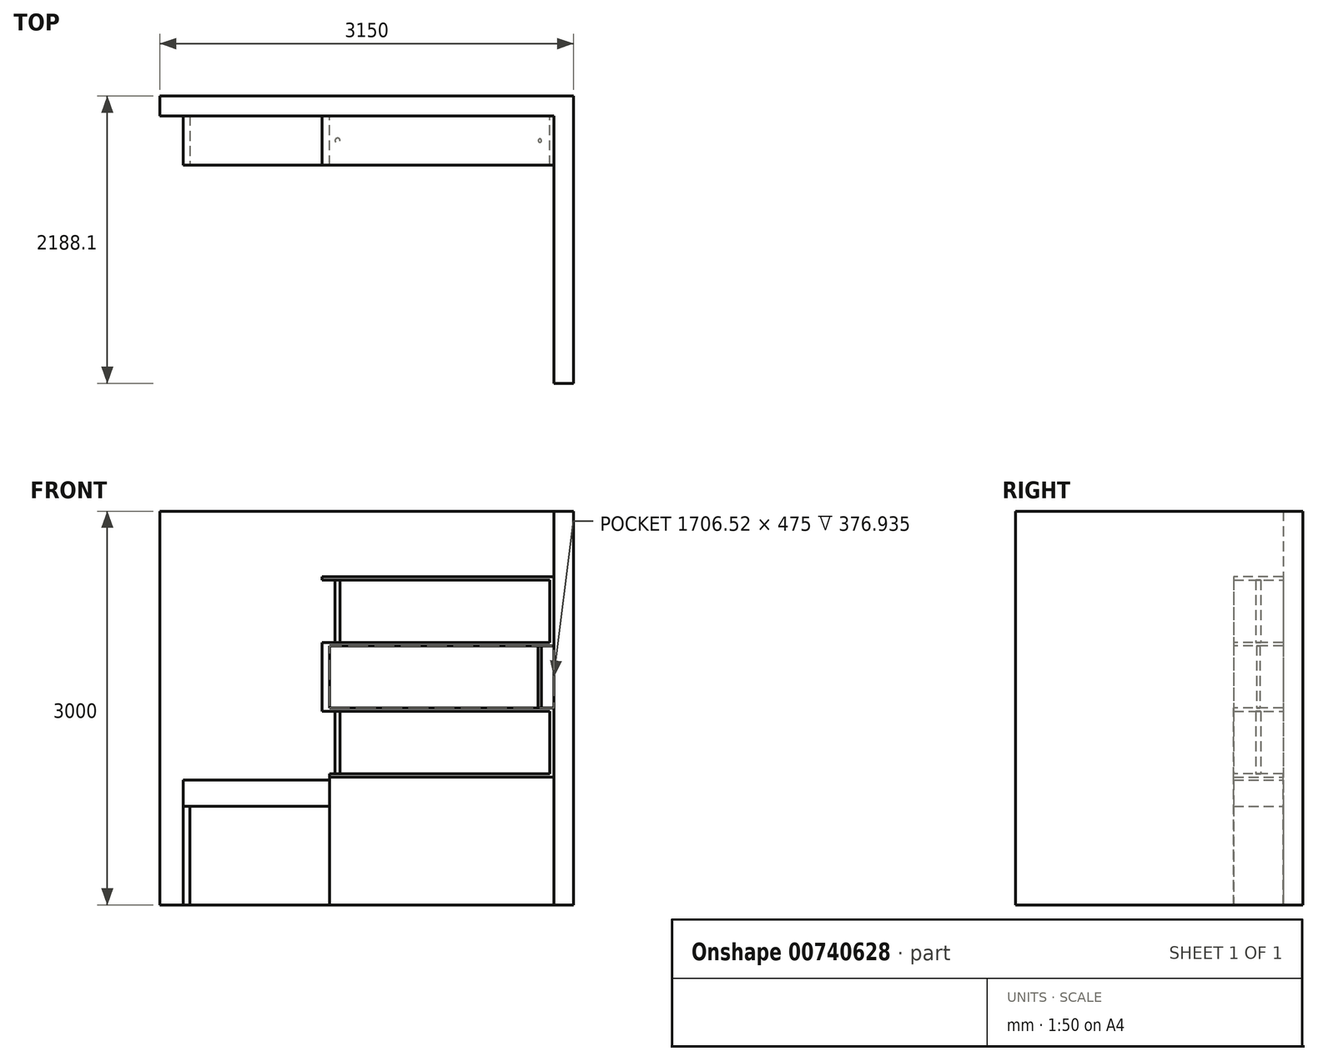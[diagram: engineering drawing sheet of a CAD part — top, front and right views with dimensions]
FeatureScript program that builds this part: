
annotation { "Feature Type Name" : "Feature", "Feature Type Description" : "" }
export const myFeature = defineFeature(function(context is Context, id is Id, definition is map)
    precondition{}
    {
        {
            var Q0;
            Q0=qCreatedBy(makeId("Top.planeOp"),FACE);
            var sketch = newSketch(context, id + "F0", { "sketchPlane" : qUnion([Q0])});
            skLineSegment(sketch, "E0", {"start": v(-3000, 0) * mm, "end": v(0, 0) * mm});
            skLineSegment(sketch, "E1", {"start": v(0, 0) * mm, "end": v(0, -2038.1) * mm});
            skLineSegment(sketch, "E2.0", {"start": v(150, 150) * mm, "end": v(150, -2038.1) * mm});
            skLineSegment(sketch, "E2.1", {"start": v(-3000, 150) * mm, "end": v(150, 150) * mm});
            skLineSegment(sketch, "E3", {"start": v(-3000, 150) * mm, "end": v(-3000, 0) * mm});
            skLineSegment(sketch, "E4", {"start": v(150, -2038.1) * mm, "end": v(0, -2038.1) * mm});
            skSolve(sketch);
        }
        {
            var Q0;
            Q0=makeQuery(id+"F0.imprint","IMPRINT",FACE,{"disambiguationData":[TD([[makeQuery(id+"F0.imprint","IMPRINT",EDGE,{"derivedFrom":sQuery(id+"F0.wireOp",EDGE,"E0")}),1.0]])]});
            extrude(context, id + "F1", {"entities" : qUnion([Q0]), "depth" : 3000 * mm, "offsetDistance" : 25 * mm});
        }
        {
            var Q0;
            Q0=qCreatedBy(makeId("Top.planeOp"),FACE);
            var sketch = newSketch(context, id + "F2", { "sketchPlane" : qUnion([Q0])});
            skLineSegment(sketch, "E5.bottom", {"start": v(0, 0) * mm, "end": v(-1764.44, 0) * mm});
            skLineSegment(sketch, "E5.top", {"start": v(0, -376.93) * mm, "end": v(-1764.44, -376.93) * mm});
            skLineSegment(sketch, "E5.left", {"start": v(0, 0) * mm, "end": v(0, -376.93) * mm});
            skLineSegment(sketch, "E5.right", {"start": v(-1764.44, 0) * mm, "end": v(-1764.44, -376.93) * mm});
            skLineSegment(sketch, "E6.bottom", {"start": v(0, 0) * mm, "end": v(-442.7, 0) * mm});
            skLineSegment(sketch, "E6.top", {"start": v(0, -1298.11) * mm, "end": v(-442.7, -1298.11) * mm});
            skLineSegment(sketch, "E6.left", {"start": v(0, 0) * mm, "end": v(0, -1298.11) * mm});
            skLineSegment(sketch, "E6.right", {"start": v(-442.7, 0) * mm, "end": v(-442.7, -1298.11) * mm});
            skLineSegment(sketch, "E7.bottom", {"start": v(-1764.44, -376.93) * mm, "end": v(-1706.52, -376.93) * mm});
            skLineSegment(sketch, "E7.top", {"start": v(-1764.44, 0) * mm, "end": v(-1706.52, 0) * mm});
            skLineSegment(sketch, "E7.left", {"start": v(-1764.44, -376.93) * mm, "end": v(-1764.44, 0) * mm});
            skLineSegment(sketch, "E7.right", {"start": v(-1706.52, -376.93) * mm, "end": v(-1706.52, 0) * mm});
            skLineSegment(sketch, "E8.bottom", {"start": v(-442.7, -1298.11) * mm, "end": v(0, -1298.11) * mm});
            skLineSegment(sketch, "E8.top", {"start": v(-442.7, -1257.65) * mm, "end": v(0, -1257.65) * mm});
            skLineSegment(sketch, "E8.left", {"start": v(-442.7, -1298.11) * mm, "end": v(-442.7, -1257.65) * mm});
            skLineSegment(sketch, "E8.right", {"start": v(0, -1298.11) * mm, "end": v(0, -1257.65) * mm});
            skCircle(sketch, "E9", {"center": v(-1646.7, -188.47) * mm, "radius": 19 * mm});
            skPoint(sketch, "E9.centerSnap0", {"position": v(-1706.52, -188.47) * mm});
            skCircle(sketch, "E10", {"center": v(-221.35, -1196.79) * mm, "radius": 24.23 * mm});
            skPoint(sketch, "E10.centerSnap0", {"position": v(-221.35, -1257.65) * mm});
            skLineSegment(sketch, "E11.bottom", {"start": v(0, 0) * mm, "end": v(-32.94, 0) * mm});
            skLineSegment(sketch, "E11.top", {"start": v(0, -376.93) * mm, "end": v(-32.94, -376.93) * mm});
            skLineSegment(sketch, "E11.right", {"start": v(-32.94, 0) * mm, "end": v(-32.94, -376.93) * mm});
            skCircle(sketch, "E12", {"center": v(-106.66, -188.47) * mm, "radius": 12.41 * mm});
            skPoint(sketch, "E12.centerSnap0", {"position": v(-32.94, -188.47) * mm});
            skLineSegment(sketch, "E13.bottom", {"start": v(-1706.52, 0) * mm, "end": v(-2822.53, 0) * mm});
            skLineSegment(sketch, "E13.top", {"start": v(-1706.52, -376.93) * mm, "end": v(-2822.53, -376.93) * mm});
            skLineSegment(sketch, "E13.left", {"start": v(-1706.52, 0) * mm, "end": v(-1706.52, -376.93) * mm});
            skLineSegment(sketch, "E13.right", {"start": v(-2822.53, 0) * mm, "end": v(-2822.53, -376.93) * mm});
            skLineSegment(sketch, "E14.bottom", {"start": v(-2822.53, 0) * mm, "end": v(-2770.61, 0) * mm});
            skLineSegment(sketch, "E14.top", {"start": v(-2822.53, -376.93) * mm, "end": v(-2770.61, -376.93) * mm});
            skLineSegment(sketch, "E14.right", {"start": v(-2770.61, 0) * mm, "end": v(-2770.61, -376.93) * mm});
            skSolve(sketch);
        }
        {
            var Q0;
            {var subQ0=sQuery(id+"F2.wireOp",EDGE,"E7.right");Q0=makeQuery(id+"F2.imprint","IMPRINT",FACE,{"disambiguationData":[TD([[makeQuery(id+"F2.imprint","IMPRINT",EDGE,{"derivedFrom":subQ0}),-1.0]])]});}
            var Q1;
            {var subQ5=sQuery(id+"F2.wireOp",EDGE,"E11.right");Q1=makeQuery(id+"F2.imprint","IMPRINT",FACE,{"disambiguationData":[TD([[makeQuery(id+"F2.imprint","IMPRINT",EDGE,{"derivedFrom":subQ5}),-1.0]])]});}
            var Q2;
            Q2=makeQuery(id+"F2.imprint","IMPRINT",FACE,{"disambiguationData":[TD([[makeQuery(id+"F2.imprint","IMPRINT",EDGE,{"derivedFrom":sQuery(id+"F2.wireOp",EDGE,"E9")}),1.0]])]});
            var Q3;
            {var subQ2=sQuery(id+"F2.wireOp",EDGE,"E5.left");Q3=makeQuery(id+"F2.imprint","IMPRINT",FACE,{"disambiguationData":[TD([[makeQuery(id+"F2.imprint","IMPRINT",EDGE,{"derivedFrom":subQ2}),-1.0]])]});}
            var Q4;
            Q4=makeQuery(id+"F2.imprint","IMPRINT",FACE,{"disambiguationData":[TD([[makeQuery(id+"F2.imprint","IMPRINT",EDGE,{"derivedFrom":sQuery(id+"F2.wireOp",EDGE,"E12")}),1.0]])]});
            extrude(context, id + "F3", {"entities" : qUnion([Q0, Q1, Q2, Q3, Q4]), "depth" : 2000 * mm, "offsetDistance" : 25 * mm, "hasSecondDirection" : true, "secondDirectionOppositeDirection" : false, "secondDirectionDepth" : 1975 * mm});
        }
        {
            var Q0;
            Q0=makeQuery(id+"F3.opExtrude","CAP_FACE",FACE,{"disambiguationData":[OSD([sQuery(id+"F2.wireOp",EDGE,"E5.bottom"),sQuery(id+"F2.wireOp",EDGE,"E5.top"),sQuery(id+"F2.wireOp",EDGE,"E5.left"),sQuery(id+"F2.wireOp",EDGE,"E7.right")])],"isStart":true});
            extrude(context, id + "F4", {"entities" : qUnion([Q0]), "depth" : 500 * mm, "offsetDistance" : 25 * mm, "hasSecondDirection" : true, "secondDirectionOppositeDirection" : false, "secondDirectionDepth" : 475 * mm});
        }
        {
            var Q0;
            Q0=makeQuery(id+"F4.opExtrude","CAP_FACE",FACE,{"disambiguationData":[OSD([sQuery(id+"F2.wireOp",EDGE,"E5.bottom"),sQuery(id+"F2.wireOp",EDGE,"E5.top"),sQuery(id+"F2.wireOp",EDGE,"E5.left"),sQuery(id+"F2.wireOp",EDGE,"E7.right")])],"isStart":false});
            extrude(context, id + "F5", {"entities" : qUnion([Q0]), "depth" : 500 * mm, "offsetDistance" : 25 * mm, "hasSecondDirection" : true, "secondDirectionOppositeDirection" : false, "secondDirectionDepth" : 475 * mm});
        }
        {
            var Q0;
            {var subQ0=sQuery(id+"F2.wireOp",EDGE,"E5.right");Q0=makeQuery(id+"F2.imprint","IMPRINT",FACE,{"disambiguationData":[TD([[makeQuery(id+"F2.imprint","IMPRINT",EDGE,{"derivedFrom":subQ0}),1.0]])]});}
            extrude(context, id + "F6", {"entities" : qUnion([Q0]), "operationType" : NewBodyOperationType.ADD, "depth" : 2000 * mm, "offsetDistance" : 25 * mm, "hasSecondDirection" : true, "secondDirectionOppositeDirection" : false, "secondDirectionDepth" : 1475 * mm});
        }
        {
            var Q0;
            {var subQ2=sQuery(id+"F2.wireOp",EDGE,"E5.left");Q0=makeQuery(id+"F2.imprint","IMPRINT",FACE,{"disambiguationData":[TD([[makeQuery(id+"F2.imprint","IMPRINT",EDGE,{"derivedFrom":subQ2}),-1.0]])]});}
            extrude(context, id + "F7", {"entities" : qUnion([Q0]), "operationType" : NewBodyOperationType.ADD, "depth" : 1500 * mm, "offsetDistance" : 25 * mm, "hasSecondDirection" : true, "secondDirectionOppositeDirection" : false, "secondDirectionDepth" : 1000 * mm});
        }
        {
            var Q0;
            {var subQ0=sQuery(id+"F2.wireOp",EDGE,"E7.right");var subQ1=sQuery(id+"F2.wireOp",EDGE,"E5.top");var subQ2=sQuery(id+"F2.wireOp",EDGE,"E5.bottom");Q0=makeQuery(id+"F6.boolean.opBoolean","MERGE",FACE,{"derivedFrom":[makeQuery(id+"F3.opExtrude","CAP_FACE",FACE,{"disambiguationData":[OSD([subQ2,subQ1,sQuery(id+"F2.wireOp",EDGE,"E5.left"),subQ0])],"isStart":false}),makeQuery(id+"F6.opExtrude","CAP_FACE",FACE,{"disambiguationData":[OSD([subQ2,subQ1,sQuery(id+"F2.wireOp",EDGE,"E5.right"),subQ0])],"isStart":false})]});}
            extrude(context, id + "F8", {"entities" : qUnion([Q0]), "operationType" : NewBodyOperationType.ADD, "depth" : 500 * mm, "offsetDistance" : 25 * mm, "hasSecondDirection" : true, "secondDirectionOppositeDirection" : false, "secondDirectionDepth" : 475 * mm});
        }
        {
            var Q0;
            {var subQ2=sQuery(id+"F2.wireOp",EDGE,"E5.left");Q0=makeQuery(id+"F2.imprint","IMPRINT",FACE,{"disambiguationData":[TD([[makeQuery(id+"F2.imprint","IMPRINT",EDGE,{"derivedFrom":subQ2}),-1.0]])]});}
            extrude(context, id + "F9", {"entities" : qUnion([Q0]), "operationType" : NewBodyOperationType.ADD, "depth" : 2500 * mm, "offsetDistance" : 25 * mm, "hasSecondDirection" : true, "secondDirectionOppositeDirection" : false, "secondDirectionDepth" : 2000 * mm});
        }
        {
            var Q0;
            Q0=makeQuery(id+"F2.imprint","IMPRINT",FACE,{"disambiguationData":[TD([[makeQuery(id+"F2.imprint","IMPRINT",EDGE,{"derivedFrom":sQuery(id+"F2.wireOp",EDGE,"E9")}),1.0]])]});
            extrude(context, id + "F10", {"entities" : qUnion([Q0]), "depth" : 1475 * mm, "offsetDistance" : 25 * mm, "hasSecondDirection" : true, "secondDirectionOppositeDirection" : false, "secondDirectionDepth" : 1000 * mm});
        }
        {
            var Q0;
            Q0=makeQuery(id+"F2.imprint","IMPRINT",FACE,{"disambiguationData":[TD([[makeQuery(id+"F2.imprint","IMPRINT",EDGE,{"derivedFrom":sQuery(id+"F2.wireOp",EDGE,"E12")}),1.0]])]});
            extrude(context, id + "F11", {"entities" : qUnion([Q0]), "depth" : 1975 * mm, "offsetDistance" : 25 * mm, "hasSecondDirection" : true, "secondDirectionOppositeDirection" : false, "secondDirectionDepth" : 1500 * mm});
        }
        {
            var Q0;
            Q0=makeQuery(id+"F2.imprint","IMPRINT",FACE,{"disambiguationData":[TD([[makeQuery(id+"F2.imprint","IMPRINT",EDGE,{"derivedFrom":sQuery(id+"F2.wireOp",EDGE,"E9")}),1.0]])]});
            extrude(context, id + "F12", {"entities" : qUnion([Q0]), "depth" : 2475 * mm, "offsetDistance" : 25 * mm, "hasSecondDirection" : true, "secondDirectionOppositeDirection" : false, "secondDirectionDepth" : 2000 * mm});
        }
        {
            var Q0;
            Q0=makeQuery(id+"F5.opExtrude","CAP_FACE",FACE,{"disambiguationData":[OSD([sQuery(id+"F2.wireOp",EDGE,"E5.bottom"),sQuery(id+"F2.wireOp",EDGE,"E5.top"),sQuery(id+"F2.wireOp",EDGE,"E5.left"),sQuery(id+"F2.wireOp",EDGE,"E7.right")])],"isStart":false});
            extrude(context, id + "F13", {"entities" : qUnion([Q0]), "depth" : 975 * mm, "offsetDistance" : 25 * mm});
        }
        {
            var Q0;
            {var subQ0=sQuery(id+"F2.wireOp",EDGE,"E5.right");Q0=makeQuery(id+"F2.imprint","IMPRINT",FACE,{"disambiguationData":[TD([[makeQuery(id+"F2.imprint","IMPRINT",EDGE,{"derivedFrom":subQ0}),-1.0]])]});}
            var Q1;
            {var subQ0=sQuery(id+"F2.wireOp",EDGE,"E13.right");Q1=makeQuery(id+"F2.imprint","IMPRINT",FACE,{"disambiguationData":[TD([[makeQuery(id+"F2.imprint","IMPRINT",EDGE,{"derivedFrom":subQ0}),1.0]])]});}
            var Q2;
            {var subQ0=sQuery(id+"F2.wireOp",EDGE,"E5.right");Q2=makeQuery(id+"F2.imprint","IMPRINT",FACE,{"disambiguationData":[TD([[makeQuery(id+"F2.imprint","IMPRINT",EDGE,{"derivedFrom":subQ0}),1.0]])]});}
            extrude(context, id + "F14", {"entities" : qUnion([Q0, Q1, Q2]), "depth" : 950 * mm, "offsetDistance" : 25 * mm, "hasSecondDirection" : true, "secondDirectionOppositeDirection" : false, "secondDirectionDepth" : 750 * mm});
        }
        {
            var Q0;
            {var subQ0=sQuery(id+"F2.wireOp",EDGE,"E13.right");Q0=makeQuery(id+"F2.imprint","IMPRINT",FACE,{"disambiguationData":[TD([[makeQuery(id+"F2.imprint","IMPRINT",EDGE,{"derivedFrom":subQ0}),1.0]])]});}
            extrude(context, id + "F15", {"entities" : qUnion([Q0]), "depth" : 750 * mm, "offsetDistance" : 25 * mm});
        }
    });
